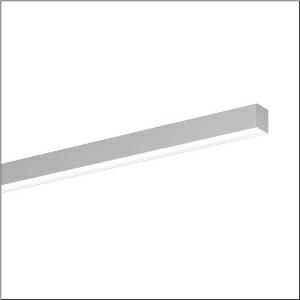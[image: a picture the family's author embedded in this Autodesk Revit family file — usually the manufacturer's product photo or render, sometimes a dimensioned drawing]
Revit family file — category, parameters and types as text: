
# Revit family: silica_21_51mx20tct5s
name_source: partatom
category: Lighting Fixtures
units: mm (PartAtom-declared; Revit-internal decimal feet)

## family parameters
Cut with Voids When Loaded = No
Host = Face
Light Source = No
Part Type = Normal
Room Calculation Point = No
Round Connector Dimension = Use Diameter
Shared = No

## types (1)
- --- (1 x LED, 6000 lm, 51.3 W, 6500K)
    Apparent Load = 51 VA
    CIE Flux Codes = 48 79 96 100 100
    Color Rendering = 80
    Color Temperature = 6500K
    Default Elevation = 1800 mm
    Description = Silica 21, office luminaire, primary optical cover: cover, of PMMA, opal, light emission: direct distribution, primary light characteristic: symmetric, installation type: surface-mounted, LED, rated luminous flux: 6.000lm, luminous efficacy: 112lm/W, light colour: 8tw, colour temperature: 2700..6500K, control gear: DALI DT8, with terminal, 3+2-pole, max. 2.5mm², mains connection: 220..240V, AC, 50/60Hz, rated input power: 53.8W, luminaire housing, of aluminium, metallic grey (RAL 9006), length: 3.004mm, width: 53mm, height: 53mm, protection rating (complete): IP20, insulation class (complete): insulation class I (protective earthing), certification: CE, permissible operating ambient temperature: 0..+35°C, standard: EN 50419, packaging unit: 1 piece
    Height = 53 mm
    Lamp = 1 x LED
    Lamp Light Flux = 6000 lm
    Lamp Power = 51.3 W
    Lamp count = 1
    Length = 3004 mm
    Luminous efficacy = 117 lm/W
    Manufacturer = Siteco
    ModVariant = No
    Model = 51MX20TCT5S
    Mounting Place = Ceiling
    Mounting Type = Surface mounted
    Number of Poles = 1
    OnlyDefault = Yes
    Power Factor = 1
    Product Name = Silica 21
    Product group = office luminaire | ceiling mounted
    ProductGroupID = 301
    Protection Class = Protection class I
    Protection Degree = IP 20
    RLX_Detail_Level = 1
    RLX_Emergency_Light_Flux = 0 lm
    RLX_Emergency_Type = 0
    RLX_Emergency_Type_DB = No
    RlxData = <blob elided: 23141 chars, md5=b51ac675>
    Socket = socket
    Standby Power = 0 W
    System Light Flux = 6000 lm
    System Power = 51 W
    Type Comments = individual setting
    Type Image = l_1335933.jpg
    URL = http://relux.com
    VarID = @adj_139157
    Voltage = 0 V
    Weight = 0.00 kg
    Width = 53 mm

## geometry (parser evidence)
native form markers: Blend x4, Sweep x11
no freeform markers — native parametric forms only
